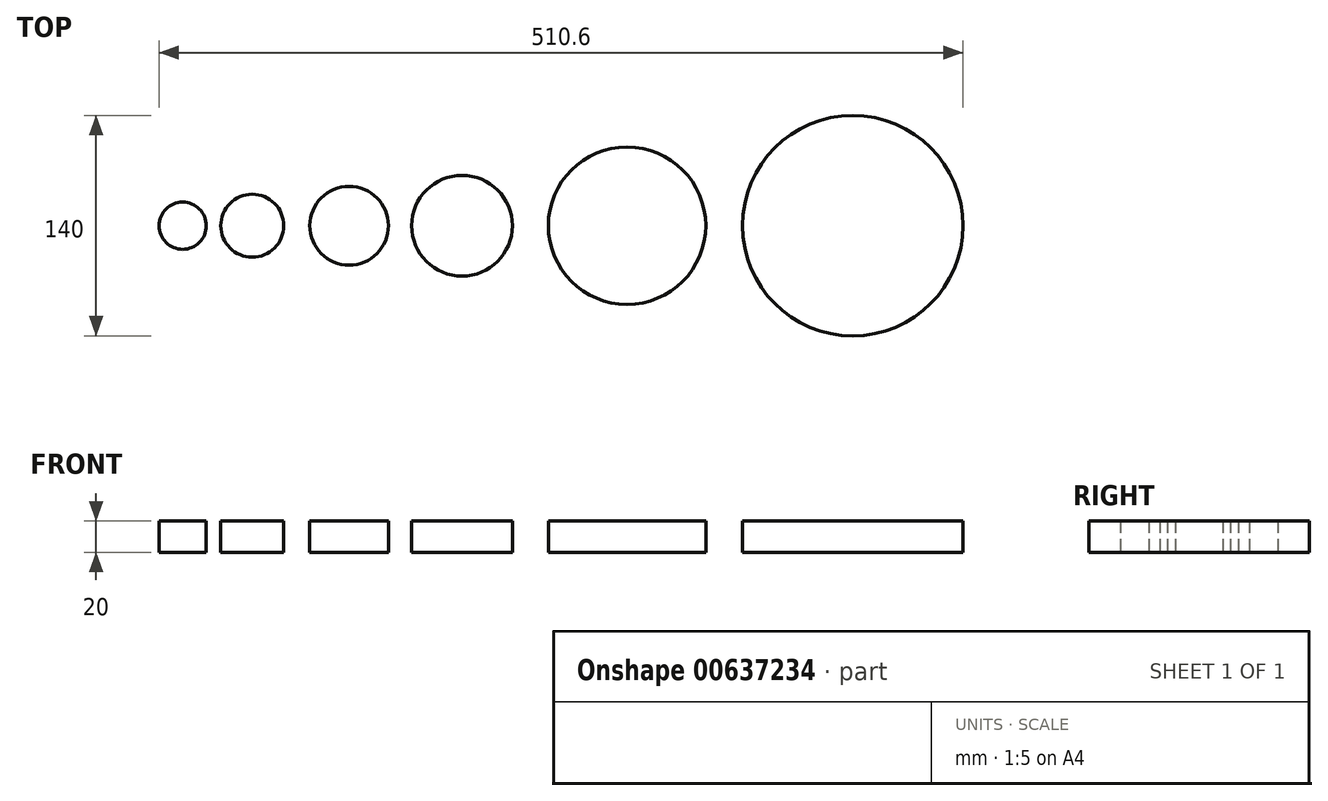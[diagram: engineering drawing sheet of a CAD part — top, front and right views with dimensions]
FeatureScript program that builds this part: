
annotation { "Feature Type Name" : "Feature", "Feature Type Description" : "" }
export const myFeature = defineFeature(function(context is Context, id is Id, definition is map)
    precondition{}
    {
        {
            var Q0;
            Q0=qCreatedBy(makeId("Top.planeOp"),FACE);
            var sketch = newSketch(context, id + "F0", { "sketchPlane" : qUnion([Q0])});
            skCircle(sketch, "E0", {"center": v(0, 0) * mm, "radius": 15 * mm});
            skSolve(sketch);
        }
        {
            var Q0;
            Q0=makeQuery(id+"F0.imprint","IMPRINT",FACE,{"disambiguationData":[TD([[makeQuery(id+"F0.imprint","IMPRINT",EDGE,{"derivedFrom":sQuery(id+"F0.wireOp",EDGE,"E0")}),1.0]])]});
            extrude(context, id + "F1", {"entities" : qUnion([Q0]), "depth" : 20 * mm, "offsetDistance" : 25 * mm});
        }
        {
            var Q0;
            Q0=qCreatedBy(makeId("Top.planeOp"),FACE);
            var sketch = newSketch(context, id + "F2", { "sketchPlane" : qUnion([Q0])});
            skCircle(sketch, "E1", {"center": v(44.2, 0) * mm, "radius": 20 * mm});
            skSolve(sketch);
        }
        {
            var Q0;
            Q0=makeQuery(id+"F2.imprint","IMPRINT",FACE,{"disambiguationData":[TD([[makeQuery(id+"F2.imprint","IMPRINT",EDGE,{"derivedFrom":sQuery(id+"F2.wireOp",EDGE,"E1")}),1.0]])]});
            extrude(context, id + "F3", {"entities" : qUnion([Q0]), "depth" : 20 * mm, "offsetDistance" : 25 * mm});
        }
        {
            var Q0;
            Q0=qCreatedBy(makeId("Top.planeOp"),FACE);
            var sketch = newSketch(context, id + "F4", { "sketchPlane" : qUnion([Q0])});
            skCircle(sketch, "E2", {"center": v(105.72, 0) * mm, "radius": 25 * mm});
            skSolve(sketch);
        }
        {
            var Q0;
            Q0=makeQuery(id+"F4.imprint","IMPRINT",FACE,{"disambiguationData":[TD([[makeQuery(id+"F4.imprint","IMPRINT",EDGE,{"derivedFrom":sQuery(id+"F4.wireOp",EDGE,"E2")}),1.0]])]});
            extrude(context, id + "F5", {"entities" : qUnion([Q0]), "depth" : 20 * mm, "offsetDistance" : 25 * mm});
        }
        {
            var Q0;
            Q0=qCreatedBy(makeId("Top.planeOp"),FACE);
            var sketch = newSketch(context, id + "F6", { "sketchPlane" : qUnion([Q0])});
            skCircle(sketch, "E3", {"center": v(177.41, 0) * mm, "radius": 32 * mm});
            skSolve(sketch);
        }
        {
            var Q0;
            Q0=makeQuery(id+"F6.imprint","IMPRINT",FACE,{"disambiguationData":[TD([[makeQuery(id+"F6.imprint","IMPRINT",EDGE,{"derivedFrom":sQuery(id+"F6.wireOp",EDGE,"E3")}),1.0]])]});
            extrude(context, id + "F7", {"entities" : qUnion([Q0]), "depth" : 20 * mm, "offsetDistance" : 25 * mm});
        }
        {
            var Q0;
            Q0=qCreatedBy(makeId("Top.planeOp"),FACE);
            var sketch = newSketch(context, id + "F8", { "sketchPlane" : qUnion([Q0])});
            skCircle(sketch, "E4", {"center": v(282.25, 0) * mm, "radius": 50 * mm});
            skSolve(sketch);
        }
        {
            var Q0;
            Q0=makeQuery(id+"F8.imprint","IMPRINT",FACE,{"disambiguationData":[TD([[makeQuery(id+"F8.imprint","IMPRINT",EDGE,{"derivedFrom":sQuery(id+"F8.wireOp",EDGE,"E4")}),1.0]])]});
            extrude(context, id + "F9", {"entities" : qUnion([Q0]), "depth" : 20 * mm, "offsetDistance" : 25 * mm});
        }
        {
            var Q0;
            Q0=qCreatedBy(makeId("Top.planeOp"),FACE);
            var sketch = newSketch(context, id + "F10", { "sketchPlane" : qUnion([Q0])});
            skCircle(sketch, "E5", {"center": v(425.6, 0) * mm, "radius": 70 * mm});
            skSolve(sketch);
        }
        {
            var Q0;
            Q0=makeQuery(id+"F10.imprint","IMPRINT",FACE,{"disambiguationData":[TD([[makeQuery(id+"F10.imprint","IMPRINT",EDGE,{"derivedFrom":sQuery(id+"F10.wireOp",EDGE,"E5")}),1.0]])]});
            extrude(context, id + "F11", {"entities" : qUnion([Q0]), "depth" : 20 * mm, "offsetDistance" : 25 * mm});
        }
    });
